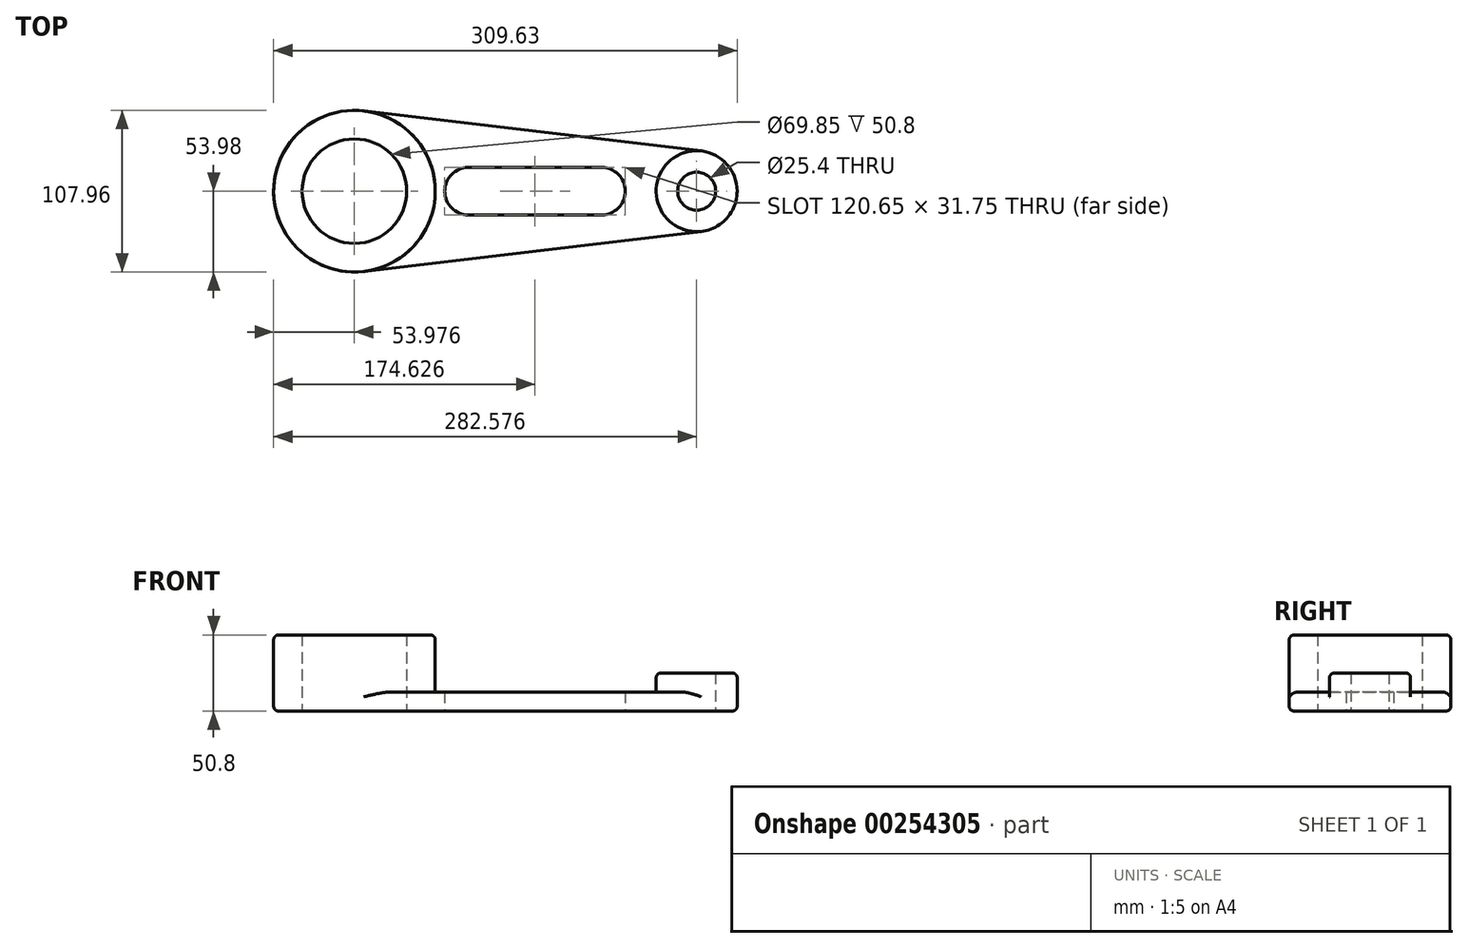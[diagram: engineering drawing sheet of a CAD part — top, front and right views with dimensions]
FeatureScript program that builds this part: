
annotation { "Feature Type Name" : "Feature", "Feature Type Description" : "" }
export const myFeature = defineFeature(function(context is Context, id is Id, definition is map)
    precondition{}
    {
        {
            var Q0;
            Q0=qCreatedBy(makeId("Top.planeOp"),FACE);
            var sketch = newSketch(context, id + "F0", { "sketchPlane" : qUnion([Q0])});
            skCircle(sketch, "E0", {"center": v(-51.44, 0) * mm, "radius": 53.98 * mm});
            skCircle(sketch, "E1", {"center": v(-51.44, 0) * mm, "radius": 34.93 * mm});
            skCircle(sketch, "E2", {"center": v(177.16, 0) * mm, "radius": 27.05 * mm});
            skCircle(sketch, "E3", {"center": v(177.16, 0) * mm, "radius": 12.7 * mm});
            skLineSegment(sketch, "E4", {"start": v(-45.09, 53.6) * mm, "end": v(180.34, 26.86) * mm});
            skLineSegment(sketch, "E5", {"start": v(-45.09, -53.6) * mm, "end": v(180.34, -26.86) * mm});
            skArc(sketch, "E6", {"start": v(24.76, 15.88) * mm, "mid": v(8.88, 0) * mm, "end": v(24.76, -15.88) * mm});
            skArc(sketch, "E7", {"start": v(113.66, -15.88) * mm, "mid": v(129.53, 0) * mm, "end": v(113.66, 15.88) * mm});
            skLineSegment(sketch, "E8", {"start": v(24.76, 15.88) * mm, "end": v(113.66, 15.88) * mm});
            skLineSegment(sketch, "E9", {"start": v(24.76, -15.88) * mm, "end": v(113.66, -15.88) * mm});
            skSolve(sketch);
        }
        {
            var Q0;
            Q0=makeQuery(id+"F0.imprint","IMPRINT",FACE,{"disambiguationData":[TD([[makeQuery(id+"F0.imprint","IMPRINT",EDGE,{"derivedFrom":sQuery(id+"F0.wireOp",EDGE,"E1")}),-1.0]])]});
            extrude(context, id + "F1", {"entities" : qUnion([Q0]), "depth" : 50.8 * mm});
        }
        {
            var Q0;
            Q0=makeQuery(id+"F0.imprint","IMPRINT",FACE,{"disambiguationData":[TD([[makeQuery(id+"F0.imprint","IMPRINT",EDGE,{"derivedFrom":sQuery(id+"F0.wireOp",EDGE,"E3")}),-1.0]])]});
            extrude(context, id + "F2", {"entities" : qUnion([Q0]), "depth" : 25.4 * mm});
        }
        {
            var Q0;
            {var subQ1=sQuery(id+"F0.wireOp",EDGE,"E4");Q0=makeQuery(id+"F0.imprint","IMPRINT",FACE,{"disambiguationData":[TD([[makeQuery(id+"F0.imprint","IMPRINT",EDGE,{"derivedFrom":subQ1}),-1.0]])]});}
            extrude(context, id + "F3", {"entities" : qUnion([Q0]), "operationType" : NewBodyOperationType.ADD, "depth" : 12.7 * mm});
        }
        {
            var Q0;
            Q0=makeQuery(id+"F3.opExtrude","CAP_EDGE",EDGE,{"disambiguationData":[OSD([sQuery(id+"F0.wireOp",EDGE,"E5")])],"isStart":true});
            var Q1;
            Q1=makeQuery(id+"F1.opExtrude","CAP_EDGE",EDGE,{"disambiguationData":[OSD([sQuery(id+"F0.wireOp",EDGE,"E0")])],"isStart":false});
            var Q2;
            Q2=makeQuery(id+"F2.opExtrude","CAP_EDGE",EDGE,{"disambiguationData":[OSD([sQuery(id+"F0.wireOp",EDGE,"E2")])],"isStart":false});
            var Q3;
            Q3=makeQuery(id+"F3.opExtrude","CAP_EDGE",EDGE,{"disambiguationData":[OSD([sQuery(id+"F0.wireOp",EDGE,"E4")])],"isStart":false});
            var Q4;
            Q4=makeQuery(id+"F3.opExtrude","CAP_EDGE",EDGE,{"disambiguationData":[OSD([sQuery(id+"F0.wireOp",EDGE,"E5")])],"isStart":false});
            var Q5;
            Q5=makeQuery(id+"F3.opExtrude","CAP_EDGE",EDGE,{"disambiguationData":[OSD([sQuery(id+"F0.wireOp",EDGE,"E0")])],"isStart":false});
            var Q6;
            Q6=makeQuery(id+"F3.opExtrude","CAP_EDGE",EDGE,{"disambiguationData":[OSD([sQuery(id+"F0.wireOp",EDGE,"E2")])],"isStart":false});
            fillet(context, id + "F4", {"entities" : qUnion([Q0, Q1, Q2, Q3, Q4, Q5, Q6]), "radius" : 3.17 * mm, "tangentPropagation" : true, "allowEdgeOverflow" : false});
        }
    });
